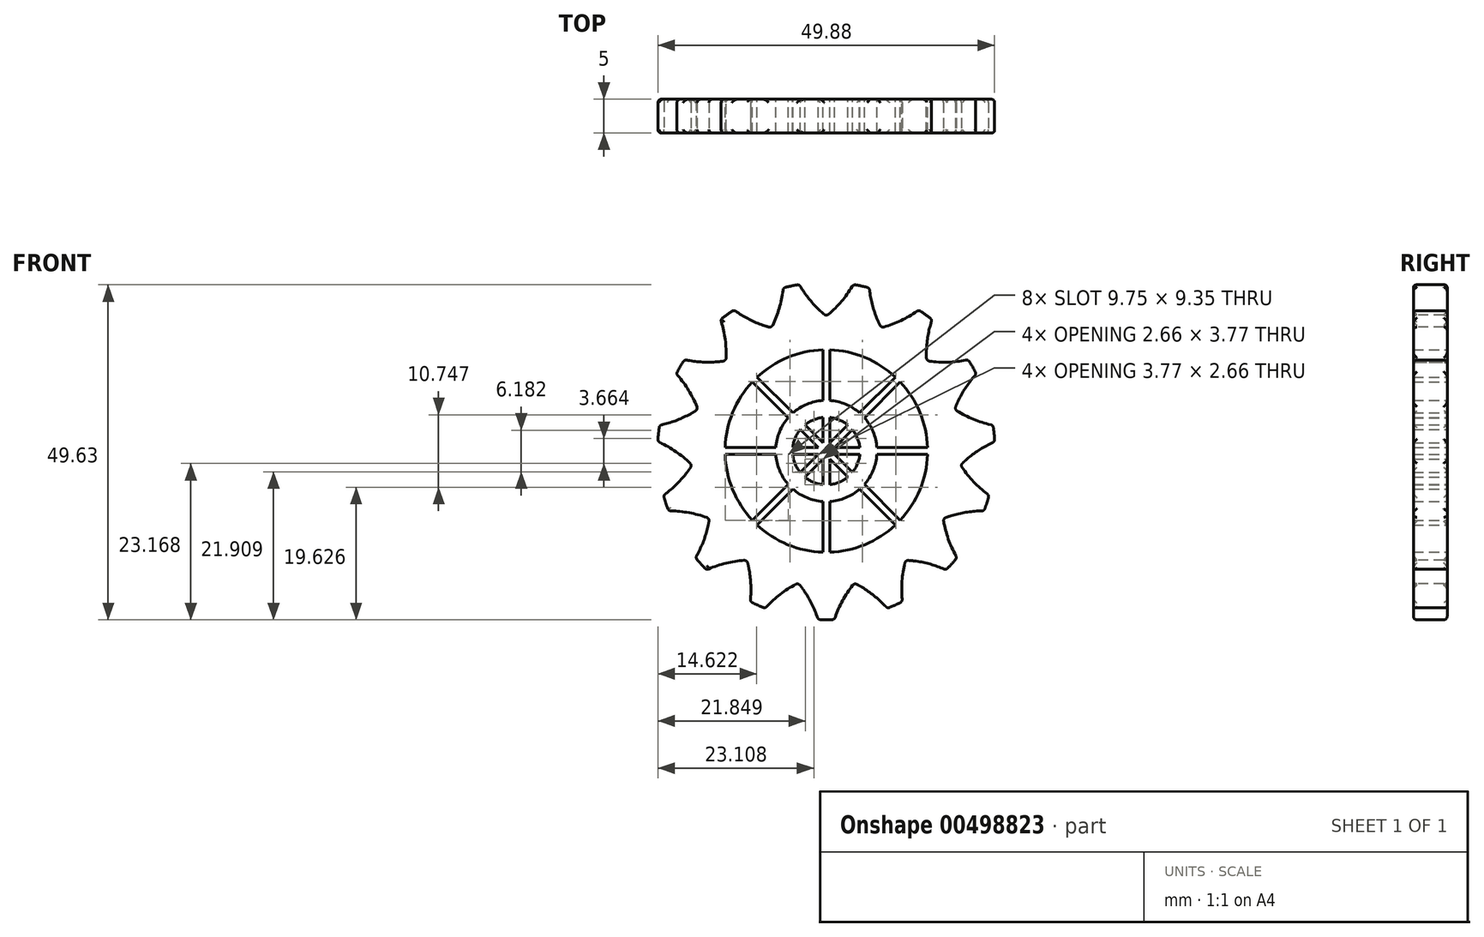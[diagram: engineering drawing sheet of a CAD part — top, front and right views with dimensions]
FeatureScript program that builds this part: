
annotation { "Feature Type Name" : "Feature", "Feature Type Description" : "" }
export const myFeature = defineFeature(function(context is Context, id is Id, definition is map)
    precondition{}
    {
        {
            var Q0;
            Q0=qCreatedBy(makeId("Front.planeOp"),FACE);
            var sketch = newSketch(context, id + "F0", { "sketchPlane" : qUnion([Q0])});
            skCircle(sketch, "E0", {"center": v(0, 0) * mm, "radius": 25 * mm});
            skArc(sketch, "E1", {"start": v(0, 20) * mm, "mid": v(2.22, 22.15) * mm, "end": v(4, 24.68) * mm});
            skArc(sketch, "E2.MirrorCS", {"start": v(0, 20) * mm, "mid": v(-2.22, 22.15) * mm, "end": v(-4, 24.68) * mm});
            skArc(sketch, "E3", {"start": v(10.25, 10.95) * mm, "mid": v(5.74, 13.86) * mm, "end": v(0.5, 15) * mm});
            skArc(sketch, "E4", {"start": v(3.16, 3.87) * mm, "mid": v(1.91, 4.62) * mm, "end": v(0.5, 4.97) * mm});
            skLineSegment(sketch, "E5", {"start": v(10.25, -10.95) * mm, "end": v(4.94, -5.65) * mm});
            skLineSegment(sketch, "E6", {"start": v(10.25, 10.95) * mm, "end": v(4.94, 5.65) * mm});
            skLineSegment(sketch, "E7", {"start": v(15, -0.5) * mm, "end": v(7.48, -0.5) * mm});
            skLineSegment(sketch, "E8.MirrorCS", {"start": v(15, 0.5) * mm, "end": v(7.48, 0.5) * mm});
            skLineSegment(sketch, "E9.MirrorCS", {"start": v(10.95, 10.25) * mm, "end": v(5.65, 4.94) * mm});
            skLineSegment(sketch, "E10", {"start": v(-0.5, 15) * mm, "end": v(-0.5, 7.48) * mm});
            skLineSegment(sketch, "E11.MirrorCS", {"start": v(0.5, 15) * mm, "end": v(0.5, 7.48) * mm});
            skLineSegment(sketch, "E12.MirrorCS", {"start": v(10.95, -10.25) * mm, "end": v(5.65, -4.94) * mm});
            skLineSegment(sketch, "E13.trimOffspring", {"start": v(-0.5, 1.2) * mm, "end": v(-3.16, 3.87) * mm});
            skLineSegment(sketch, "E14.trimOffspring", {"start": v(-1.2, 0.5) * mm, "end": v(-4.97, 0.5) * mm});
            skLineSegment(sketch, "E15.trimOffspring", {"start": v(-1.2, 0.5) * mm, "end": v(-3.87, 3.16) * mm});
            skLineSegment(sketch, "E16.trimOffspring", {"start": v(-1.2, -0.5) * mm, "end": v(-3.87, -3.16) * mm});
            skLineSegment(sketch, "E17.trimOffspring", {"start": v(-1.2, -0.5) * mm, "end": v(-4.97, -0.5) * mm});
            skLineSegment(sketch, "E18.trimOffspring", {"start": v(-0.5, -1.2) * mm, "end": v(-0.5, -4.97) * mm});
            skLineSegment(sketch, "E19.trimOffspring", {"start": v(-0.5, -1.2) * mm, "end": v(-3.16, -3.87) * mm});
            skLineSegment(sketch, "E20.trimOffspring", {"start": v(0.5, -1.2) * mm, "end": v(0.5, -4.97) * mm});
            skArc(sketch, "E21.trimOffspring", {"start": v(-0.5, 15) * mm, "mid": v(-5.74, 13.86) * mm, "end": v(-10.25, 10.95) * mm});
            skArc(sketch, "E22.trimOffspring", {"start": v(-10.95, 10.25) * mm, "mid": v(-13.86, 5.74) * mm, "end": v(-15, 0.5) * mm});
            skArc(sketch, "E23.trimOffspring", {"start": v(-15, -0.5) * mm, "mid": v(-13.86, -5.74) * mm, "end": v(-10.95, -10.25) * mm});
            skArc(sketch, "E24.trimOffspring", {"start": v(-10.25, -10.95) * mm, "mid": v(-5.74, -13.86) * mm, "end": v(-0.5, -15) * mm});
            skArc(sketch, "E25.trimOffspring", {"start": v(0.5, -15) * mm, "mid": v(5.74, -13.86) * mm, "end": v(10.25, -10.95) * mm});
            skArc(sketch, "E26.trimOffspring", {"start": v(10.95, -10.25) * mm, "mid": v(13.86, -5.74) * mm, "end": v(15, -0.5) * mm});
            skArc(sketch, "E27.trimOffspring", {"start": v(15, 0.5) * mm, "mid": v(13.86, 5.74) * mm, "end": v(10.95, 10.25) * mm});
            skArc(sketch, "E28.trimOffspring", {"start": v(-0.5, 4.97) * mm, "mid": v(-1.91, 4.62) * mm, "end": v(-3.16, 3.87) * mm});
            skArc(sketch, "E29.trimOffspring", {"start": v(-3.87, 3.16) * mm, "mid": v(-4.62, 1.91) * mm, "end": v(-4.97, 0.5) * mm});
            skArc(sketch, "E30.trimOffspring", {"start": v(-4.97, -0.5) * mm, "mid": v(-4.62, -1.91) * mm, "end": v(-3.87, -3.16) * mm});
            skArc(sketch, "E31.trimOffspring", {"start": v(-3.16, -3.87) * mm, "mid": v(-1.91, -4.62) * mm, "end": v(-0.5, -4.97) * mm});
            skArc(sketch, "E32.trimOffspring", {"start": v(0.5, -4.97) * mm, "mid": v(1.91, -4.62) * mm, "end": v(3.16, -3.87) * mm});
            skArc(sketch, "E33.trimOffspring", {"start": v(3.87, -3.16) * mm, "mid": v(4.62, -1.91) * mm, "end": v(4.97, -0.5) * mm});
            skArc(sketch, "E34.trimOffspring", {"start": v(4.97, 0.5) * mm, "mid": v(4.62, 1.91) * mm, "end": v(3.87, 3.16) * mm});
            skArc(sketch, "E35", {"start": v(4.94, 5.65) * mm, "mid": v(2.87, 6.93) * mm, "end": v(0.5, 7.48) * mm});
            skLineSegment(sketch, "E36.trimOffspring", {"start": v(3.16, 3.87) * mm, "end": v(0.5, 1.2) * mm});
            skLineSegment(sketch, "E37.trimOffspring", {"start": v(3.87, 3.16) * mm, "end": v(1.2, 0.5) * mm});
            skLineSegment(sketch, "E38.trimOffspring", {"start": v(0.5, 4.97) * mm, "end": v(0.5, 1.2) * mm});
            skLineSegment(sketch, "E39.trimOffspring", {"start": v(-0.5, 4.97) * mm, "end": v(-0.5, 1.2) * mm});
            skArc(sketch, "E40.trimOffspring", {"start": v(-0.5, 7.48) * mm, "mid": v(-2.87, 6.93) * mm, "end": v(-4.94, 5.65) * mm});
            skArc(sketch, "E41.trimOffspring", {"start": v(-5.65, 4.94) * mm, "mid": v(-6.93, 2.87) * mm, "end": v(-7.48, 0.5) * mm});
            skLineSegment(sketch, "E42.trimOffspring", {"start": v(-4.94, 5.65) * mm, "end": v(-10.25, 10.95) * mm});
            skLineSegment(sketch, "E43.trimOffspring", {"start": v(-5.65, 4.94) * mm, "end": v(-10.95, 10.25) * mm});
            skLineSegment(sketch, "E44.trimOffspring", {"start": v(-7.48, 0.5) * mm, "end": v(-15, 0.5) * mm});
            skArc(sketch, "E45.trimOffspring", {"start": v(-7.48, -0.5) * mm, "mid": v(-6.93, -2.87) * mm, "end": v(-5.65, -4.94) * mm});
            skLineSegment(sketch, "E46.trimOffspring", {"start": v(-7.48, -0.5) * mm, "end": v(-15, -0.5) * mm});
            skLineSegment(sketch, "E47.trimOffspring", {"start": v(-5.65, -4.94) * mm, "end": v(-10.95, -10.25) * mm});
            skLineSegment(sketch, "E48.trimOffspring", {"start": v(-4.94, -5.65) * mm, "end": v(-10.25, -10.95) * mm});
            skArc(sketch, "E49.trimOffspring", {"start": v(-4.94, -5.65) * mm, "mid": v(-2.87, -6.93) * mm, "end": v(-0.5, -7.48) * mm});
            skArc(sketch, "E50.trimOffspring", {"start": v(0.5, -7.48) * mm, "mid": v(2.87, -6.93) * mm, "end": v(4.94, -5.65) * mm});
            skLineSegment(sketch, "E51.trimOffspring", {"start": v(0.5, -7.48) * mm, "end": v(0.5, -15) * mm});
            skLineSegment(sketch, "E52.trimOffspring", {"start": v(-0.5, -7.48) * mm, "end": v(-0.5, -15) * mm});
            skLineSegment(sketch, "E53.trimOffspring", {"start": v(3.16, -3.87) * mm, "end": v(0.5, -1.2) * mm});
            skLineSegment(sketch, "E54.trimOffspring", {"start": v(3.87, -3.16) * mm, "end": v(1.2, -0.5) * mm});
            skArc(sketch, "E55.trimOffspring", {"start": v(5.65, -4.94) * mm, "mid": v(6.93, -2.87) * mm, "end": v(7.48, -0.5) * mm});
            skArc(sketch, "E56.trimOffspring", {"start": v(7.48, 0.5) * mm, "mid": v(6.93, 2.87) * mm, "end": v(5.65, 4.94) * mm});
            skLineSegment(sketch, "E57.trimOffspring", {"start": v(4.97, 0.5) * mm, "end": v(1.2, 0.5) * mm});
            skLineSegment(sketch, "E58.trimOffspring", {"start": v(4.97, -0.5) * mm, "end": v(1.2, -0.5) * mm});
            skSolve(sketch);
        }
        {
            var Q0;
            {var subQ0=sQuery(id+"F0.wireOp",EDGE,"E1");Q0=makeQuery(id+"F0.imprint","IMPRINT",FACE,{"disambiguationData":[TD([[makeQuery(id+"F0.imprint","IMPRINT",EDGE,{"derivedFrom":subQ0}),-1.0]])]});}
            extrude(context, id + "F1", {"entities" : qUnion([Q0]), "depth" : 5 * mm, "offsetDistance" : 25 * mm});
        }
        {
            var Q0;
            {var subQ0=sQuery(id+"F0.wireOp",EDGE,"E1");Q0=makeQuery(id+"F0.imprint","IMPRINT",FACE,{"disambiguationData":[TD([[makeQuery(id+"F0.imprint","IMPRINT",EDGE,{"derivedFrom":subQ0}),1.0]])]});}
            extrude(context, id + "F2", {"entities" : qUnion([Q0]), "endBound" : BoundingType.SYMMETRIC, "depth" : 25 * mm, "offsetDistance" : 25 * mm});
        }
        {
            var Q0;
            Q0=makeQuery(id+"F2.opExtrude","SWEPT_BODY",BODY,{"disambiguationData":[OSD([sQuery(id+"F0.wireOp",EDGE,"E0"),sQuery(id+"F0.wireOp",EDGE,"LOeSV7sq-UWMy-6uDd-izUR-KJthB2q1vHRz"),sQuery(id+"F0.wireOp",EDGE,"cdd84428-3e49-451f-bbc9-1467798db5890.MirrorCS")])]});
            var Q1;
            Q1=makeQuery(id+"F1.opExtrude","CAP_EDGE",EDGE,{"disambiguationData":[OSD([sQuery(id+"F0.wireOp",EDGE,"E0")])],"isStart":false});
            circularPattern(context, id + "F3", {"operationType" : NewBodyOperationType.REMOVE, "entities" : qUnion([Q0]), "axis" : qUnion([Q1]), "angle" : 360 * degree, "instanceCount" : 15, "equalSpace" : true});
        }
        {
            var Q0;
            Q0=makeQuery(id+"F3.boolean.opBoolean","COPY",FACE,{"derivedFrom":makeQuery(id+"F3.opPattern","COPY",FACE,{"derivedFrom":makeQuery(id+"F2.opExtrude","SWEPT_FACE",FACE,{"disambiguationData":[OSD([sQuery(id+"F0.wireOp",EDGE,"E1")])]}),"instanceName":"12"})});
            var Q1;
            Q1=makeQuery(id+"F3.boolean.opBoolean","COPY",FACE,{"derivedFrom":makeQuery(id+"F3.opPattern","COPY",FACE,{"derivedFrom":makeQuery(id+"F2.opExtrude","SWEPT_FACE",FACE,{"disambiguationData":[OSD([sQuery(id+"F0.wireOp",EDGE,"E1")])]}),"instanceName":"13"})});
            var Q2;
            Q2=makeQuery(id+"F3.boolean.opBoolean","COPY",FACE,{"derivedFrom":makeQuery(id+"F3.opPattern","COPY",FACE,{"derivedFrom":makeQuery(id+"F2.opExtrude","SWEPT_FACE",FACE,{"disambiguationData":[OSD([sQuery(id+"F0.wireOp",EDGE,"E1")])]}),"instanceName":"14"})});
            var Q3;
            Q3=makeQuery(id+"F1.opExtrude","SWEPT_FACE",FACE,{"disambiguationData":[OSD([sQuery(id+"F0.wireOp",EDGE,"E1")])]});
            var Q4;
            Q4=makeQuery(id+"F3.boolean.opBoolean","COPY",FACE,{"derivedFrom":makeQuery(id+"F3.opPattern","COPY",FACE,{"derivedFrom":makeQuery(id+"F2.opExtrude","SWEPT_FACE",FACE,{"disambiguationData":[OSD([sQuery(id+"F0.wireOp",EDGE,"E1")])]}),"instanceName":"1"})});
            var Q5;
            Q5=makeQuery(id+"F3.boolean.opBoolean","COPY",FACE,{"derivedFrom":makeQuery(id+"F3.opPattern","COPY",FACE,{"derivedFrom":makeQuery(id+"F2.opExtrude","SWEPT_FACE",FACE,{"disambiguationData":[OSD([sQuery(id+"F0.wireOp",EDGE,"E1")])]}),"instanceName":"2"})});
            var Q6;
            Q6=makeQuery(id+"F3.boolean.opBoolean","COPY",FACE,{"derivedFrom":makeQuery(id+"F3.opPattern","COPY",FACE,{"derivedFrom":makeQuery(id+"F2.opExtrude","SWEPT_FACE",FACE,{"disambiguationData":[OSD([sQuery(id+"F0.wireOp",EDGE,"E1")])]}),"instanceName":"3"})});
            var Q7;
            Q7=makeQuery(id+"F3.boolean.opBoolean","COPY",FACE,{"derivedFrom":makeQuery(id+"F3.opPattern","COPY",FACE,{"derivedFrom":makeQuery(id+"F2.opExtrude","SWEPT_FACE",FACE,{"disambiguationData":[OSD([sQuery(id+"F0.wireOp",EDGE,"E1")])]}),"instanceName":"4"})});
            var Q8;
            Q8=makeQuery(id+"F3.boolean.opBoolean","COPY",FACE,{"derivedFrom":makeQuery(id+"F3.opPattern","COPY",FACE,{"derivedFrom":makeQuery(id+"F2.opExtrude","SWEPT_FACE",FACE,{"disambiguationData":[OSD([sQuery(id+"F0.wireOp",EDGE,"E1")])]}),"instanceName":"5"})});
            var Q9;
            Q9=makeQuery(id+"F3.boolean.opBoolean","COPY",FACE,{"derivedFrom":makeQuery(id+"F3.opPattern","COPY",FACE,{"derivedFrom":makeQuery(id+"F2.opExtrude","SWEPT_FACE",FACE,{"disambiguationData":[OSD([sQuery(id+"F0.wireOp",EDGE,"E1")])]}),"instanceName":"6"})});
            var Q10;
            Q10=makeQuery(id+"F3.boolean.opBoolean","COPY",FACE,{"derivedFrom":makeQuery(id+"F3.opPattern","COPY",FACE,{"derivedFrom":makeQuery(id+"F2.opExtrude","SWEPT_FACE",FACE,{"disambiguationData":[OSD([sQuery(id+"F0.wireOp",EDGE,"E1")])]}),"instanceName":"7"})});
            var Q11;
            Q11=makeQuery(id+"F3.boolean.opBoolean","COPY",FACE,{"derivedFrom":makeQuery(id+"F3.opPattern","COPY",FACE,{"derivedFrom":makeQuery(id+"F2.opExtrude","SWEPT_FACE",FACE,{"disambiguationData":[OSD([sQuery(id+"F0.wireOp",EDGE,"E1")])]}),"instanceName":"8"})});
            var Q12;
            Q12=makeQuery(id+"F3.boolean.opBoolean","COPY",FACE,{"derivedFrom":makeQuery(id+"F3.opPattern","COPY",FACE,{"derivedFrom":makeQuery(id+"F2.opExtrude","SWEPT_FACE",FACE,{"disambiguationData":[OSD([sQuery(id+"F0.wireOp",EDGE,"E1")])]}),"instanceName":"9"})});
            var Q13;
            Q13=makeQuery(id+"F3.boolean.opBoolean","COPY",FACE,{"derivedFrom":makeQuery(id+"F3.opPattern","COPY",FACE,{"derivedFrom":makeQuery(id+"F2.opExtrude","SWEPT_FACE",FACE,{"disambiguationData":[OSD([sQuery(id+"F0.wireOp",EDGE,"E1")])]}),"instanceName":"10"})});
            var Q14;
            Q14=makeQuery(id+"F3.boolean.opBoolean","COPY",FACE,{"derivedFrom":makeQuery(id+"F3.opPattern","COPY",FACE,{"derivedFrom":makeQuery(id+"F2.opExtrude","SWEPT_FACE",FACE,{"disambiguationData":[OSD([sQuery(id+"F0.wireOp",EDGE,"E1")])]}),"instanceName":"11"})});
            var Q15;
            {var subQ56=sQuery(id+"F0.wireOp",EDGE,"E2.MirrorCS");var subQ58=sQuery(id+"F0.wireOp",EDGE,"E0");Q15=makeQuery(id+"F3.boolean.opBoolean","SPLIT",FACE,{"disambiguationData":[TD([makeQuery(id+"F3.opPattern","COPY",FACE,{"derivedFrom":makeQuery(id+"F2.opExtrude","SWEPT_FACE",FACE,{"disambiguationData":[OSD([subQ56])]}),"instanceName":"7"})])],"derivedFrom":makeQuery(id+"F1.opExtrude","SWEPT_FACE",FACE,{"disambiguationData":[OSD([subQ58])]})});}
            var Q16;
            {var subQ56=sQuery(id+"F0.wireOp",EDGE,"E2.MirrorCS");var subQ58=sQuery(id+"F0.wireOp",EDGE,"E0");Q16=makeQuery(id+"F3.boolean.opBoolean","SPLIT",FACE,{"disambiguationData":[TD([makeQuery(id+"F3.opPattern","COPY",FACE,{"derivedFrom":makeQuery(id+"F2.opExtrude","SWEPT_FACE",FACE,{"disambiguationData":[OSD([subQ56])]}),"instanceName":"6"})])],"derivedFrom":makeQuery(id+"F1.opExtrude","SWEPT_FACE",FACE,{"disambiguationData":[OSD([subQ58])]})});}
            var Q17;
            {var subQ56=sQuery(id+"F0.wireOp",EDGE,"E2.MirrorCS");var subQ58=sQuery(id+"F0.wireOp",EDGE,"E0");Q17=makeQuery(id+"F3.boolean.opBoolean","SPLIT",FACE,{"disambiguationData":[TD([makeQuery(id+"F3.opPattern","COPY",FACE,{"derivedFrom":makeQuery(id+"F2.opExtrude","SWEPT_FACE",FACE,{"disambiguationData":[OSD([subQ56])]}),"instanceName":"5"})])],"derivedFrom":makeQuery(id+"F1.opExtrude","SWEPT_FACE",FACE,{"disambiguationData":[OSD([subQ58])]})});}
            var Q18;
            {var subQ56=sQuery(id+"F0.wireOp",EDGE,"E2.MirrorCS");var subQ58=sQuery(id+"F0.wireOp",EDGE,"E0");Q18=makeQuery(id+"F3.boolean.opBoolean","SPLIT",FACE,{"disambiguationData":[TD([makeQuery(id+"F3.opPattern","COPY",FACE,{"derivedFrom":makeQuery(id+"F2.opExtrude","SWEPT_FACE",FACE,{"disambiguationData":[OSD([subQ56])]}),"instanceName":"4"})])],"derivedFrom":makeQuery(id+"F1.opExtrude","SWEPT_FACE",FACE,{"disambiguationData":[OSD([subQ58])]})});}
            var Q19;
            {var subQ56=sQuery(id+"F0.wireOp",EDGE,"E2.MirrorCS");var subQ58=sQuery(id+"F0.wireOp",EDGE,"E0");Q19=makeQuery(id+"F3.boolean.opBoolean","SPLIT",FACE,{"disambiguationData":[TD([makeQuery(id+"F3.opPattern","COPY",FACE,{"derivedFrom":makeQuery(id+"F2.opExtrude","SWEPT_FACE",FACE,{"disambiguationData":[OSD([subQ56])]}),"instanceName":"2"})])],"derivedFrom":makeQuery(id+"F1.opExtrude","SWEPT_FACE",FACE,{"disambiguationData":[OSD([subQ58])]})});}
            var Q20;
            {var subQ56=sQuery(id+"F0.wireOp",EDGE,"E2.MirrorCS");var subQ58=sQuery(id+"F0.wireOp",EDGE,"E0");Q20=makeQuery(id+"F3.boolean.opBoolean","SPLIT",FACE,{"disambiguationData":[TD([makeQuery(id+"F3.opPattern","COPY",FACE,{"derivedFrom":makeQuery(id+"F2.opExtrude","SWEPT_FACE",FACE,{"disambiguationData":[OSD([subQ56])]}),"instanceName":"3"})])],"derivedFrom":makeQuery(id+"F1.opExtrude","SWEPT_FACE",FACE,{"disambiguationData":[OSD([subQ58])]})});}
            var Q21;
            {var subQ56=sQuery(id+"F0.wireOp",EDGE,"E2.MirrorCS");var subQ58=sQuery(id+"F0.wireOp",EDGE,"E0");Q21=makeQuery(id+"F3.boolean.opBoolean","SPLIT",FACE,{"disambiguationData":[TD([makeQuery(id+"F3.opPattern","COPY",FACE,{"derivedFrom":makeQuery(id+"F2.opExtrude","SWEPT_FACE",FACE,{"disambiguationData":[OSD([subQ56])]}),"instanceName":"1"})])],"derivedFrom":makeQuery(id+"F1.opExtrude","SWEPT_FACE",FACE,{"disambiguationData":[OSD([subQ58])]})});}
            var Q22;
            {var subQ56=sQuery(id+"F0.wireOp",EDGE,"E2.MirrorCS");var subQ58=sQuery(id+"F0.wireOp",EDGE,"E0");Q22=makeQuery(id+"F3.boolean.opBoolean","SPLIT",FACE,{"disambiguationData":[TD([makeQuery(id+"F1.opExtrude","SWEPT_FACE",FACE,{"disambiguationData":[OSD([subQ56])]})])],"derivedFrom":makeQuery(id+"F1.opExtrude","SWEPT_FACE",FACE,{"disambiguationData":[OSD([subQ58])]})});}
            var Q23;
            {var subQ57=sQuery(id+"F0.wireOp",EDGE,"E1");var subQ58=sQuery(id+"F0.wireOp",EDGE,"E0");Q23=makeQuery(id+"F3.boolean.opBoolean","SPLIT",FACE,{"disambiguationData":[TD([makeQuery(id+"F1.opExtrude","SWEPT_FACE",FACE,{"disambiguationData":[OSD([subQ57])]})])],"derivedFrom":makeQuery(id+"F1.opExtrude","SWEPT_FACE",FACE,{"disambiguationData":[OSD([subQ58])]})});}
            var Q24;
            {var subQ56=sQuery(id+"F0.wireOp",EDGE,"E2.MirrorCS");var subQ58=sQuery(id+"F0.wireOp",EDGE,"E0");Q24=makeQuery(id+"F3.boolean.opBoolean","SPLIT",FACE,{"disambiguationData":[TD([makeQuery(id+"F3.opPattern","COPY",FACE,{"derivedFrom":makeQuery(id+"F2.opExtrude","SWEPT_FACE",FACE,{"disambiguationData":[OSD([subQ56])]}),"instanceName":"13"})])],"derivedFrom":makeQuery(id+"F1.opExtrude","SWEPT_FACE",FACE,{"disambiguationData":[OSD([subQ58])]})});}
            var Q25;
            {var subQ56=sQuery(id+"F0.wireOp",EDGE,"E2.MirrorCS");var subQ58=sQuery(id+"F0.wireOp",EDGE,"E0");Q25=makeQuery(id+"F3.boolean.opBoolean","SPLIT",FACE,{"disambiguationData":[TD([makeQuery(id+"F3.opPattern","COPY",FACE,{"derivedFrom":makeQuery(id+"F2.opExtrude","SWEPT_FACE",FACE,{"disambiguationData":[OSD([subQ56])]}),"instanceName":"12"})])],"derivedFrom":makeQuery(id+"F1.opExtrude","SWEPT_FACE",FACE,{"disambiguationData":[OSD([subQ58])]})});}
            var Q26;
            {var subQ56=sQuery(id+"F0.wireOp",EDGE,"E2.MirrorCS");var subQ58=sQuery(id+"F0.wireOp",EDGE,"E0");Q26=makeQuery(id+"F3.boolean.opBoolean","SPLIT",FACE,{"disambiguationData":[TD([makeQuery(id+"F3.opPattern","COPY",FACE,{"derivedFrom":makeQuery(id+"F2.opExtrude","SWEPT_FACE",FACE,{"disambiguationData":[OSD([subQ56])]}),"instanceName":"11"})])],"derivedFrom":makeQuery(id+"F1.opExtrude","SWEPT_FACE",FACE,{"disambiguationData":[OSD([subQ58])]})});}
            var Q27;
            {var subQ56=sQuery(id+"F0.wireOp",EDGE,"E2.MirrorCS");var subQ58=sQuery(id+"F0.wireOp",EDGE,"E0");Q27=makeQuery(id+"F3.boolean.opBoolean","SPLIT",FACE,{"disambiguationData":[TD([makeQuery(id+"F3.opPattern","COPY",FACE,{"derivedFrom":makeQuery(id+"F2.opExtrude","SWEPT_FACE",FACE,{"disambiguationData":[OSD([subQ56])]}),"instanceName":"10"})])],"derivedFrom":makeQuery(id+"F1.opExtrude","SWEPT_FACE",FACE,{"disambiguationData":[OSD([subQ58])]})});}
            var Q28;
            {var subQ56=sQuery(id+"F0.wireOp",EDGE,"E2.MirrorCS");var subQ58=sQuery(id+"F0.wireOp",EDGE,"E0");Q28=makeQuery(id+"F3.boolean.opBoolean","SPLIT",FACE,{"disambiguationData":[TD([makeQuery(id+"F3.opPattern","COPY",FACE,{"derivedFrom":makeQuery(id+"F2.opExtrude","SWEPT_FACE",FACE,{"disambiguationData":[OSD([subQ56])]}),"instanceName":"9"})])],"derivedFrom":makeQuery(id+"F1.opExtrude","SWEPT_FACE",FACE,{"disambiguationData":[OSD([subQ58])]})});}
            var Q29;
            {var subQ56=sQuery(id+"F0.wireOp",EDGE,"E2.MirrorCS");var subQ58=sQuery(id+"F0.wireOp",EDGE,"E0");Q29=makeQuery(id+"F3.boolean.opBoolean","SPLIT",FACE,{"disambiguationData":[TD([makeQuery(id+"F3.opPattern","COPY",FACE,{"derivedFrom":makeQuery(id+"F2.opExtrude","SWEPT_FACE",FACE,{"disambiguationData":[OSD([subQ56])]}),"instanceName":"8"})])],"derivedFrom":makeQuery(id+"F1.opExtrude","SWEPT_FACE",FACE,{"disambiguationData":[OSD([subQ58])]})});}
            fillet(context, id + "F4", {"entities" : qUnion([Q0, Q1, Q2, Q3, Q4, Q5, Q6, Q7, Q8, Q9, Q10, Q11, Q12, Q13, Q14, Q15, Q16, Q17, Q18, Q19, Q20, Q21, Q22, Q23, Q24, Q25, Q26, Q27, Q28, Q29]), "tangentPropagation" : true, "radius" : .5 * mm, "defaultsChanged" : false, "vertexSettings" : [], "allowEdgeOverflow" : false});
        }
    });
